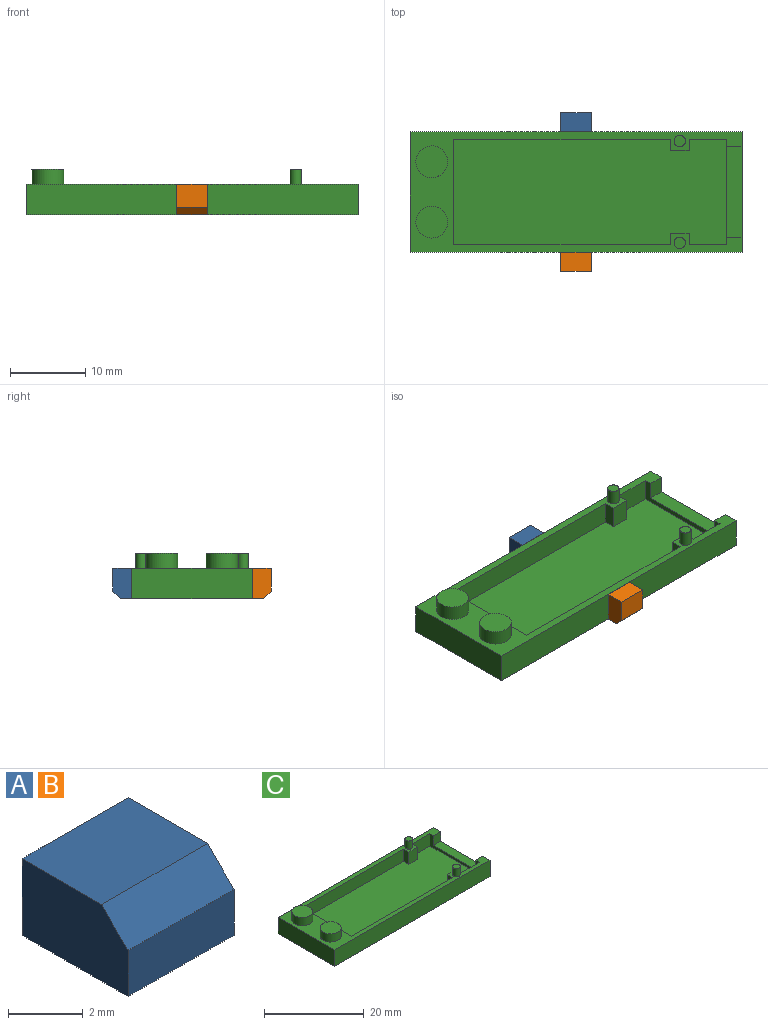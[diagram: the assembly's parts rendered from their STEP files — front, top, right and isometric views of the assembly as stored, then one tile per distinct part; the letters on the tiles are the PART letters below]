
ASSEMBLY  parts=3 mates=2
PART A: 7 faces, bbox 4x4x2.5 mm
  f0: plane 4x2.5mm, normal (-1,0,0), area 9.5mm2, adj f1,f3,f4,f5,f6
  f1: plane 4x1.5mm, normal (0,-1,0), area 6mm2, adj f0,f2,f5,f6
  f2: plane 4x2.5mm, normal (1,0,0), area 9.5mm2, adj f1,f3,f4,f5,f6
  f3: plane 4x2.5mm, normal (0,1,0), area 10mm2, adj f0,f2,f4,f5
  f4: plane 4x3mm, normal (0,0,1), area 12mm2, adj f0,f2,f3,f6
  f5: plane 4x4mm, normal (0,0,-1), area 16mm2, adj f0,f1,f2,f3
  f6: plane 4x1mm, normal (0,-0.71,0.71), area 5.7mm2, adj f0,f1,f2,f4
PART B: same geometry as A
PART C: 30 faces, bbox 44x16x6 mm
  f0: plane 36.21x14mm, normal (0,0,1), area 499.4mm2, adj f1,f2,f4,f5,f6,f15,f16,f17
  f1: plane 28.71x3mm, normal (0,1,0), area 86.1mm2, adj f0,f12,f20,f21
  f2: plane 28.71x3mm, normal (0,-1,0), area 86.1mm2, adj f0,f12,f15,f21
  f3: plane 2.33x2mm, normal (0,1,0), area 4.7mm2, adj f6,f8,f12,f14
  f4: plane 5x3mm, normal (0,1,0), area 15mm2, adj f0,f6,f12,f18
  f5: plane 5x3mm, normal (0,-1,0), area 15mm2, adj f0,f6,f12,f16
  f6: plane 14x3mm, normal (-1,0,0), area 14mm2, adj f0,f3,f4,f5,f7,f12,f14
  f7: plane 2.33x2mm, normal (0,-1,0), area 4.7mm2, adj f6,f8,f12,f14
  f8: plane 16x4mm, normal (1,0,0), area 36mm2, adj f3,f7,f9,f11,f12,f13,f14
  f9: plane 44x4mm, normal (0,1,0), area 176mm2, adj f8,f10,f12,f13
  f10: plane 16x4mm, normal (-1,0,0), area 64mm2, adj f9,f11,f12,f13
  f11: plane 44x4mm, normal (0,-1,0), area 176mm2, adj f8,f10,f12,f13
  f12: plane 44x16mm, normal (0,0,1), area 149.2mm2, adj f1,f2,f3,f4,f5,f6,f7,f8
  f13: plane 44x16mm, normal (0,0,-1), area 704mm2, adj f8,f9,f10,f11
  f14: plane 12x2mm, normal (0,0,1), area 24mm2, adj f3,f6,f7,f8
  f15: plane 3x1.5mm, normal (-1,0,0), area 4.5mm2, adj f0,f2,f12,f17
  f16: plane 3x1.5mm, normal (1,0,0), area 4.5mm2, adj f0,f5,f12,f17
  f17: plane 3x2.5mm, normal (0,-1,0), area 7.5mm2, adj f0,f12,f15,f16
  f18: plane 3x1.5mm, normal (1,0,0), area 4.5mm2, adj f0,f4,f12,f19
  f19: plane 3x2.5mm, normal (0,1,0), area 7.5mm2, adj f0,f12,f18,f20
  f20: plane 3x1.5mm, normal (-1,0,0), area 4.5mm2, adj f0,f1,f12,f19
  f21: plane 14x3mm, normal (1,0,0), area 42mm2, adj f0,f1,f2,f12
  f22: cylinder r=2.1mm len=4.21mm, axis (0,0,-1), area 26.4mm2, adj f12,f23
  f23: plane 4.21x4.21mm, normal (0,0,1), area 13.9mm2, adj f22
  f24: cylinder r=2.1mm len=4.21mm, axis (0,0,-1), area 26.4mm2, adj f12,f25
  f25: plane 4.21x4.21mm, normal (0,0,1), area 13.9mm2, adj f24
  f26: cylinder r=0.75mm len=2mm, axis (0,0,-1), area 9.4mm2, adj f12,f27
  f27: plane 1.5x1.5mm, normal (0,0,1), area 1.8mm2, adj f26
  f28: cylinder r=0.75mm len=2mm, axis (0,0,-1), area 9.4mm2, adj f12,f29
  f29: plane 1.5x1.5mm, normal (0,0,1), area 1.8mm2, adj f28
PLACE A rot(axis=(0,-0.71,-0.71),180deg) t=(27.33,19.08,1.49)mm
PLACE B rot(axis=(1,0,0),90deg) t=(23.33,3.08,1.49)mm
PLACE C t=(5.33,4.08,1.49)mm
MATE parallel A.f5 <-> C.f9  axis (0,-1,0) through (25.33,19.08,3.49)mm
MATE parallel B.f5 <-> C.f11  axis (0,1,0) through (25.33,3.08,3.49)mm
